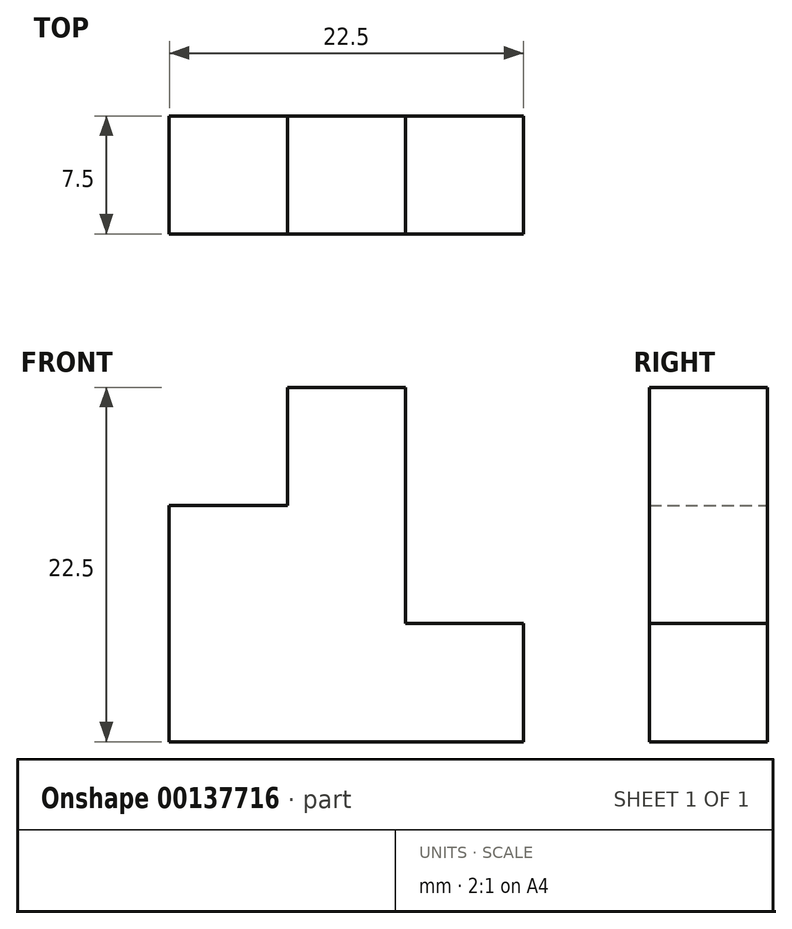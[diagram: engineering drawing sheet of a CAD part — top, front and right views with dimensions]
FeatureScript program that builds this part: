
annotation { "Feature Type Name" : "Feature", "Feature Type Description" : "" }
export const myFeature = defineFeature(function(context is Context, id is Id, definition is map)
    precondition{}
    {
        {
            var Q0;
            Q0=qCreatedBy(makeId("Front.planeOp"),FACE);
            var sketch = newSketch(context, id + "F0", { "sketchPlane" : qUnion([Q0])});
            skLineSegment(sketch, "E0", {"start": v(-17.94, 15) * mm, "end": v(-17.94, 0) * mm});
            skLineSegment(sketch, "E1", {"start": v(-17.94, 0) * mm, "end": v(4.56, 0) * mm});
            skLineSegment(sketch, "E2", {"start": v(4.56, 0) * mm, "end": v(4.56, 7.5) * mm});
            skLineSegment(sketch, "E3", {"start": v(4.56, 7.5) * mm, "end": v(-2.94, 7.5) * mm});
            skLineSegment(sketch, "E4", {"start": v(-2.94, 7.5) * mm, "end": v(-2.94, 22.5) * mm});
            skLineSegment(sketch, "E5", {"start": v(-2.94, 22.5) * mm, "end": v(-10.44, 22.5) * mm});
            skLineSegment(sketch, "E6", {"start": v(-10.44, 22.5) * mm, "end": v(-10.44, 15) * mm});
            skLineSegment(sketch, "E7", {"start": v(-17.94, 15) * mm, "end": v(-10.44, 15) * mm});
            skSolve(sketch);
        }
        {
            var Q0;
            Q0=makeQuery(id+"F0.imprint","IMPRINT",FACE,{"disambiguationData":[TD([[makeQuery(id+"F0.imprint","IMPRINT",EDGE,{"derivedFrom":sQuery(id+"F0.wireOp",EDGE,"E0")}),1.0]])]});
            extrude(context, id + "F1", {"entities" : qUnion([Q0]), "depth" : 7.5 * mm});
        }
    });
